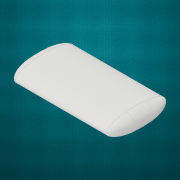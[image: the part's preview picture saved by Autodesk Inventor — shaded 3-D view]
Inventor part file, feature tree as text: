
AUTODESK INVENTOR PART (.ipt)
format: ipt  version: 2017 (Build 210142000, 142)  size: 325,120 bytes
history: native  units: in
note: dims shown in document units (in); Inventor stores cm internally (conversion verified against a paired STEP export)
features: extrude x1, fillet x1, sketch x1
ambient origin geometry x8: Origin, YZ Plane, XZ Plane, XY Plane, X Axis, Y Axis, Z Axis, Center Point
bodies: Solid1 (feature_tree)
feature tree (3):
  extrude  "Extrusion1"  Depth=8.0in
  fillet  "Fillet1"  Radius=29.5in
  sketch  "Sketch1"  dims[d0=2.5in d1=8.0in d2=29.5in d3=0.0in d4=2.375in]
